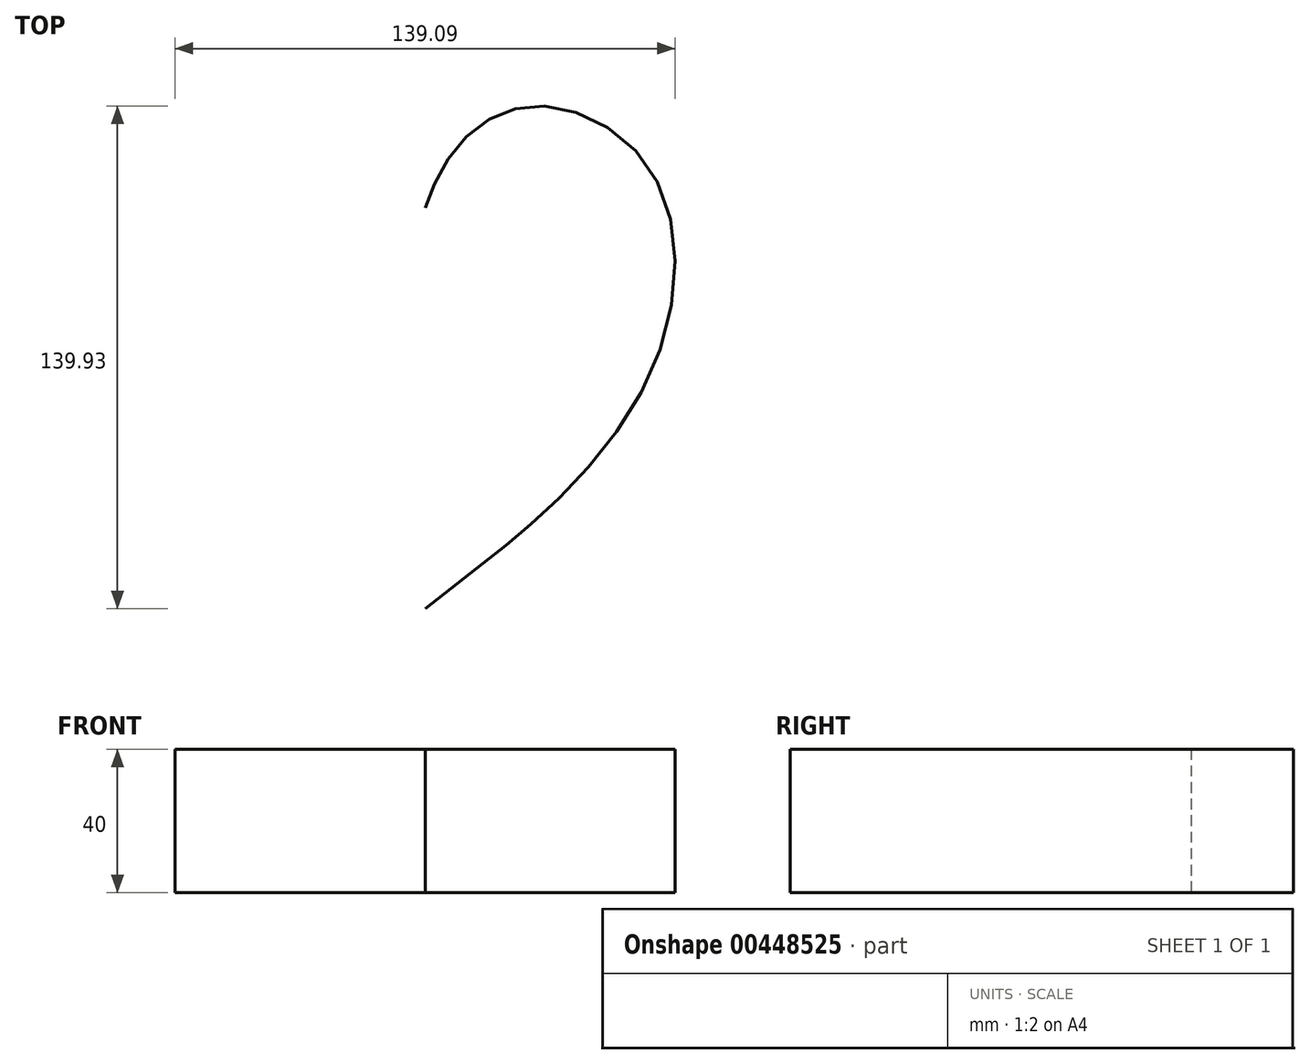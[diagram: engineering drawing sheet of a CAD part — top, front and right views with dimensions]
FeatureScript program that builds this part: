
annotation { "Feature Type Name" : "Feature", "Feature Type Description" : "" }
export const myFeature = defineFeature(function(context is Context, id is Id, definition is map)
    precondition{}
    {
        {
            var Q0;
            Q0=qCreatedBy(makeId("Top.planeOp"),FACE);
            var sketch = newSketch(context, id + "F0", { "sketchPlane" : qUnion([Q0])});
            skLineSegment(sketch, "E0", {"start": v(2.56, 36.8) * mm, "end": v(-183.57, 36.8) * mm, "construction": true});
            skLineSegment(sketch, "E1", {"start": v(2.56, 36.8) * mm, "end": v(157.98, 36.8) * mm, "construction": true});
            skFitSpline(sketch, "E2", {"points": [v(2.63, 8.53) * mm, v(-9.07, 28.5) * mm, v(-31.63, 36.8) * mm, v(-61.5, 16.74) * mm, v(-60.14, -37.44) * mm, v(-24.9, -81.19) * mm, v(2.63, -103) * mm], "startDerivative": vector(-43.82, 145.7) * mm, "endDerivative": vector(235.36, -190.2) * mm});
            skLineSegment(sketch, "E3", {"start": v(2.63, -103) * mm, "end": v(2.63, 28.57) * mm, "construction": true});
            skFitSpline(sketch, "E4.MirrorCS", {"points": [v(2.63, 8.53) * mm, v(14.32, 28.5) * mm, v(36.89, 36.8) * mm, v(66.75, 16.74) * mm, v(65.4, -37.44) * mm, v(30.15, -81.19) * mm, v(2.63, -103) * mm], "startDerivative": vector(43.82, 145.7) * mm, "endDerivative": vector(-235.36, -190.2) * mm});
            skSolve(sketch);
        }
        {
            var Q0;
            Q0 = qSketchRegion(id + "F0", true);
            extrude(context, id + "F1", {"entities" : qUnion([Q0]), "depth" : 40 * mm});
        }
    });
